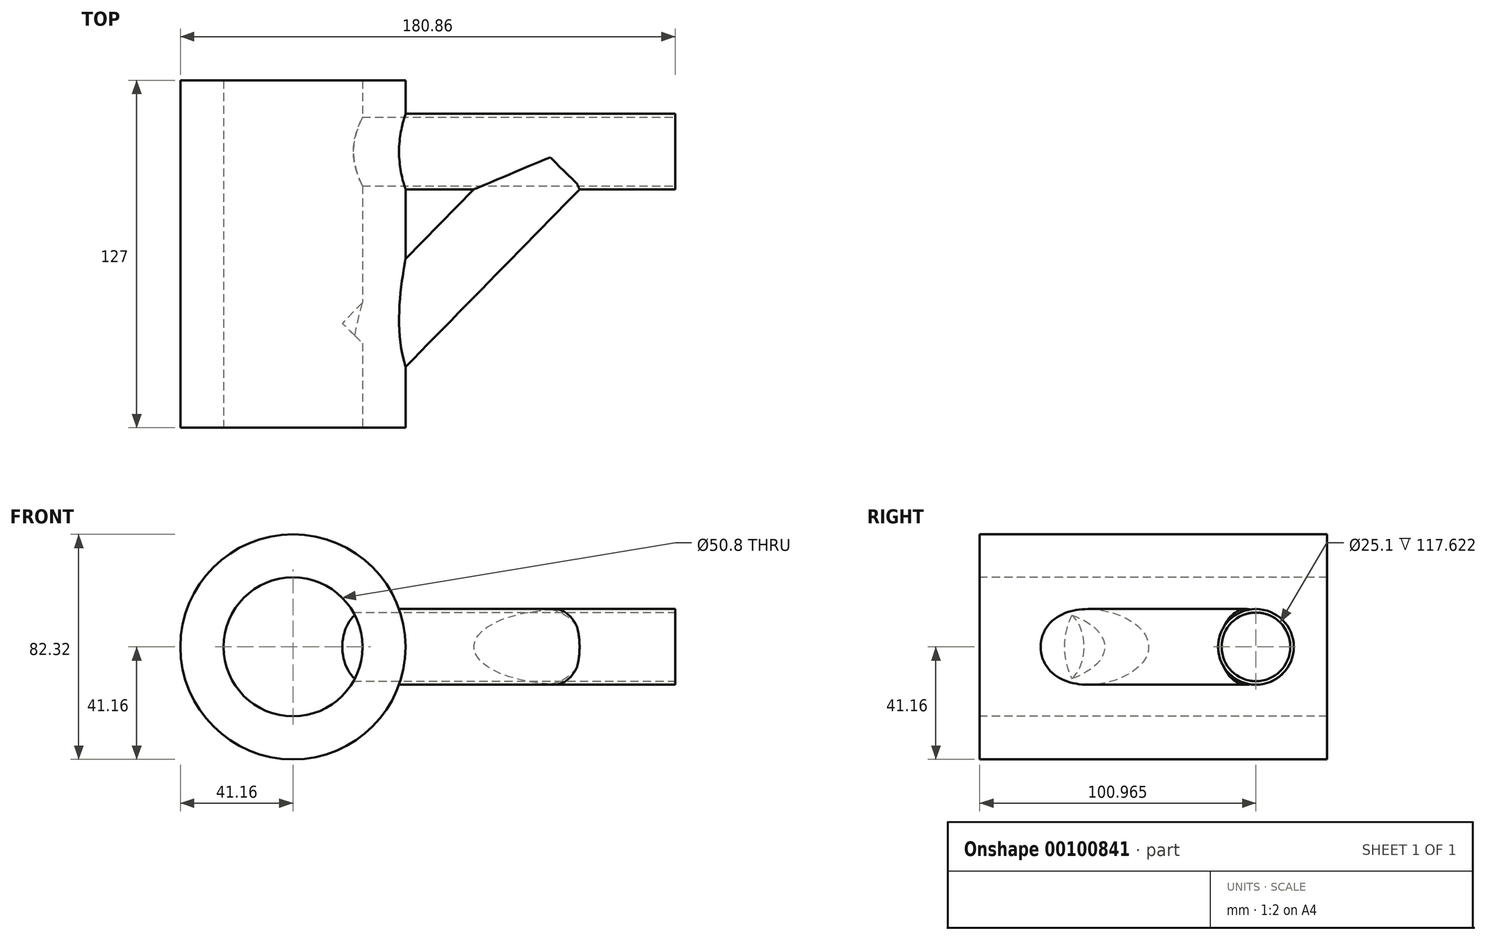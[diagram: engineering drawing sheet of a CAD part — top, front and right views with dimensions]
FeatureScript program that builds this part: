
annotation { "Feature Type Name" : "Feature", "Feature Type Description" : "" }
export const myFeature = defineFeature(function(context is Context, id is Id, definition is map)
    precondition{}
    {
        {
            var Q0;
            Q0=qCreatedBy(makeId("Front.planeOp"),FACE);
            var sketch = newSketch(context, id + "F0", { "sketchPlane" : qUnion([Q0])});
            skCircle(sketch, "E0", {"center": v(0, 0) * mm, "radius": 41.16 * mm});
            skSolve(sketch);
        }
        {
            var Q0;
            Q0 = qSketchRegion(id + "F0", true);
            extrude(context, id + "F1", {"entities" : qUnion([Q0]), "oppositeDirection" : true, "depth" : 127 * mm});
        }
        {
            var Q0;
            Q0=qCreatedBy(makeId("Right.planeOp"),FACE);
            var sketch = newSketch(context, id + "F2", { "sketchPlane" : qUnion([Q0])});
            skCircle(sketch, "E1", {"center": v(100.97, 0) * mm, "radius": 13.83 * mm});
            skSolve(sketch);
        }
        {
            var Q0;
            Q0 = qSketchRegion(id + "F2", true);
            extrude(context, id + "F3", {"entities" : qUnion([Q0]), "operationType" : NewBodyOperationType.ADD, "depth" : 139.7 * mm});
        }
        {
            var Q0;
            Q0=makeQuery(id+"F1.opExtrude","CAP_FACE",FACE,{"disambiguationData":[OSD([sQuery(id+"F0.wireOp",EDGE,"E0")])],"isStart":true});
            var sketch = newSketch(context, id + "F4", { "sketchPlane" : qUnion([Q0])});
            skCircle(sketch, "E2", {"center": v(0, 0) * mm, "radius": 25.4 * mm});
            skSolve(sketch);
        }
        {
            var Q0;
            Q0 = qSketchRegion(id + "F4", true);
            extrude(context, id + "F5", {"entities" : qUnion([Q0]), "operationType" : NewBodyOperationType.REMOVE, "endBound" : BoundingType.THROUGH_ALL, "oppositeDirection" : true, "depth" : 25.4 * mm});
        }
        {
            var Q0;
            Q0=makeQuery(id+"F3.opExtrude","CAP_FACE",FACE,{"disambiguationData":[OSD([sQuery(id+"F2.wireOp",EDGE,"E1")])],"isStart":false});
            var sketch = newSketch(context, id + "F6", { "sketchPlane" : qUnion([Q0])});
            skCircle(sketch, "E3", {"center": v(100.97, 0) * mm, "radius": 12.55 * mm});
            skSolve(sketch);
        }
        {
            var Q0;
            Q0=qCreatedBy(makeId("Top.planeOp"),FACE);
            var sketch = newSketch(context, id + "F7", { "sketchPlane" : qUnion([Q0])});
            skLineSegment(sketch, "E4", {"start": v(0, 0) * mm, "end": v(91.35, 93.23) * mm, "construction": true});
            skSolve(sketch);
        }
        {
            var Q0;
            Q0=sQuery(id+"F7.wireOp",EDGE,"E4");
            cPlane(context, id + "F8", {"entities" : qUnion([Q0]), "cplaneType" : CPlaneType.MID_PLANE, "offset" : 152.4 * mm, "width" : 152.4 * mm, "height" : 152.4 * mm});
        }
        {
            var Q0;
            Q0=qCreatedBy(id+"F8.planeOp",FACE);
            var sketch = newSketch(context, id + "F9", { "sketchPlane" : qUnion([Q0])});
            skCircle(sketch, "E5", {"center": v(0, 0) * mm, "radius": 13.83 * mm});
            skSolve(sketch);
        }
        {
            var Q0;
            Q0 = qSketchRegion(id + "F9", true);
            extrude(context, id + "F10", {"entities" : qUnion([Q0]), "operationType" : NewBodyOperationType.ADD, "depth" : 71.12 * mm, "hasSecondDirection" : true, "secondDirectionOppositeDirection" : true, "secondDirectionDepth" : 25.4 * mm});
        }
        {
            var Q0;
            Q0=makeQuery(id+"F6.imprint","IMPRINT",FACE,{"disambiguationData":[TD([[makeQuery(id+"F6.imprint","IMPRINT",EDGE,{"derivedFrom":sQuery(id+"F6.wireOp",EDGE,"E3")}),1.0]])]});
            extrude(context, id + "F11", {"entities" : qUnion([Q0]), "operationType" : NewBodyOperationType.REMOVE, "oppositeDirection" : true, "depth" : 130.13 * mm});
        }
    });
